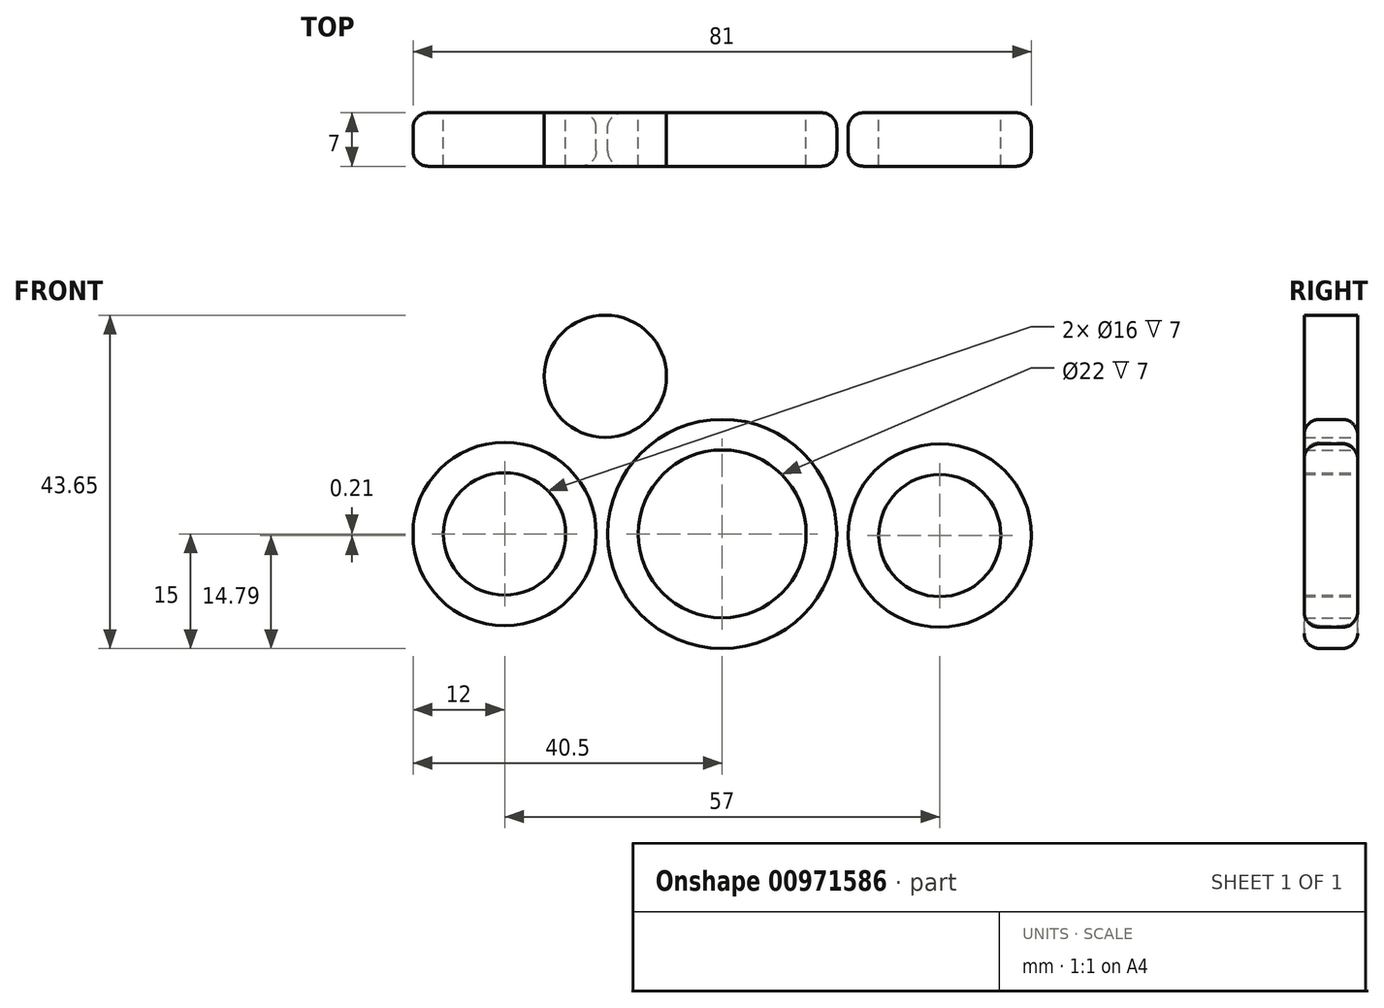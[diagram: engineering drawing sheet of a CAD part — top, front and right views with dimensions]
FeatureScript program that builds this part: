
annotation { "Feature Type Name" : "Feature", "Feature Type Description" : "" }
export const myFeature = defineFeature(function(context is Context, id is Id, definition is map)
    precondition{}
    {
        {
            var Q0;
            Q0=qCreatedBy(makeId("Front.planeOp"),FACE);
            var sketch = newSketch(context, id + "F0", { "sketchPlane" : qUnion([Q0])});
            skCircle(sketch, "E0", {"center": v(0, 0) * mm, "radius": 15 * mm});
            skCircle(sketch, "E1", {"center": v(0, 0) * mm, "radius": 11 * mm});
            skCircle(sketch, "E2", {"center": v(28.5, -0.21) * mm, "radius": 12 * mm});
            skCircle(sketch, "E3", {"center": v(-28.5, 0) * mm, "radius": 12 * mm});
            skCircle(sketch, "E4", {"center": v(28.5, -0.21) * mm, "radius": 8 * mm});
            skCircle(sketch, "E5", {"center": v(-28.5, 0) * mm, "radius": 8 * mm});
            skFitSpline(sketch, "E6", {"points": [v(13.93, -5.57) * mm, v(15.98, -5) * mm, v(17.76, -5.57) * mm], "startDerivative": vector(4.14, 3.65) * mm, "endDerivative": vector(4.67, -3.32) * mm});
            skPoint(sketch, "E7", {"position": v(17.98, 5.57) * mm});
            skFitSpline(sketch, "E8", {"points": [v(13.93, 5.57) * mm, v(16.1, 4.34) * mm, v(17.98, 5.57) * mm], "startDerivative": vector(3.73, -5.86) * mm, "endDerivative": vector(2.95, 5.65) * mm});
            skFitSpline(sketch, "E9", {"points": [v(-17.87, 5.57) * mm, v(-15.94, 5) * mm, v(-13.93, 5.57) * mm], "startDerivative": vector(4.5, -3.24) * mm, "endDerivative": vector(3.97, 3.57) * mm});
            skFitSpline(sketch, "E10", {"points": [v(-17.87, -5.57) * mm, v(-15.73, -5) * mm, v(-13.87, -5.57) * mm], "startDerivative": vector(4.74, 3.25) * mm, "endDerivative": vector(3.26, -4.19) * mm});
            skSolve(sketch);
        }
        {
            var Q0;
            Q0 = qSketchRegion(id + "F0", true);
            extrude(context, id + "F1", {"entities" : qUnion([Q0]), "depth" : 7 * mm, "offsetDistance" : 25 * mm});
        }
        {
            var Q0;
            Q0=qCreatedBy(makeId("Front.planeOp"),FACE);
            var sketch = newSketch(context, id + "F2", { "sketchPlane" : qUnion([Q0])});
            skCircle(sketch, "E11", {"center": v(-45.81, 43.95) * mm, "radius": 8 * mm});
            skSolve(sketch);
        }
        {
            var Q0;
            Q0 = qSketchRegion(id + "F2", true);
            extrude(context, id + "F3", {"entities" : qUnion([Q0]), "depth" : 7 * mm, "offsetDistance" : 25 * mm});
        }
        {
            var Q0;
            Q0=makeQuery(id+"F1.opExtrude","SWEPT_FACE",FACE,{"disambiguationData":[OSD([sQuery(id+"F0.wireOp",EDGE,"E3")])]});
            var Q1;
            {var subQ0=sQuery(id+"F0.wireOp",EDGE,"E0");Q1=makeQuery(id+"F1.opExtrude","SWEPT_FACE",FACE,{"disambiguationData":[OSD([subQ0]),TDD([makeQuery(id+"F0.imprint","IMPRINT",EDGE,{"disambiguationData":[TD([[makeQuery(id+"F0.imprint","INTERSECT",VERTEX,{"derivedFrom":[subQ0,sQuery(id+"F0.wireOp",EDGE,"E6")]}),1.0]])],"derivedFrom":subQ0})])]});}
            var Q2;
            Q2=makeQuery(id+"F1.opExtrude","SWEPT_FACE",FACE,{"disambiguationData":[OSD([sQuery(id+"F0.wireOp",EDGE,"E2")])]});
            var Q3;
            {var subQ0=sQuery(id+"F0.wireOp",EDGE,"E0");Q3=makeQuery(id+"F1.opExtrude","CAP_EDGE",EDGE,{"disambiguationData":[OSD([subQ0]),TDD([makeQuery(id+"F0.imprint","IMPRINT",EDGE,{"disambiguationData":[TD([[makeQuery(id+"F0.imprint","INTERSECT",VERTEX,{"derivedFrom":[subQ0,sQuery(id+"F0.wireOp",EDGE,"E8")]}),-1.0]])],"derivedFrom":subQ0})])],"isStart":true});}
            var Q4;
            {var subQ0=sQuery(id+"F0.wireOp",EDGE,"E0");Q4=makeQuery(id+"F1.opExtrude","CAP_EDGE",EDGE,{"disambiguationData":[OSD([subQ0]),TDD([makeQuery(id+"F0.imprint","IMPRINT",EDGE,{"disambiguationData":[TD([[makeQuery(id+"F0.imprint","INTERSECT",VERTEX,{"derivedFrom":[subQ0,sQuery(id+"F0.wireOp",EDGE,"E8")]}),-1.0]])],"derivedFrom":subQ0})])],"isStart":false});}
            fillet(context, id + "F4", {"entities" : qUnion([Q0, Q1, Q2, Q3, Q4]), "radius" : 2 * mm, "tangentPropagation" : true, "allowEdgeOverflow" : false});
        }
        {
            var Q0;
            Q0=makeQuery(id+"F3.opExtrude","SWEPT_BODY",BODY,{"disambiguationData":[OSD([sQuery(id+"F2.wireOp",EDGE,"E11")])]});
            transform(context, id + "F5", {"entities" : qUnion([Q0]), "transformType" : TransformType.TRANSLATION_3D, "dx" : 30.5 * mm, "dy" : 0 * mm, "dz" : -23.3 * mm, "makeCopy" : false});
        }
    });
